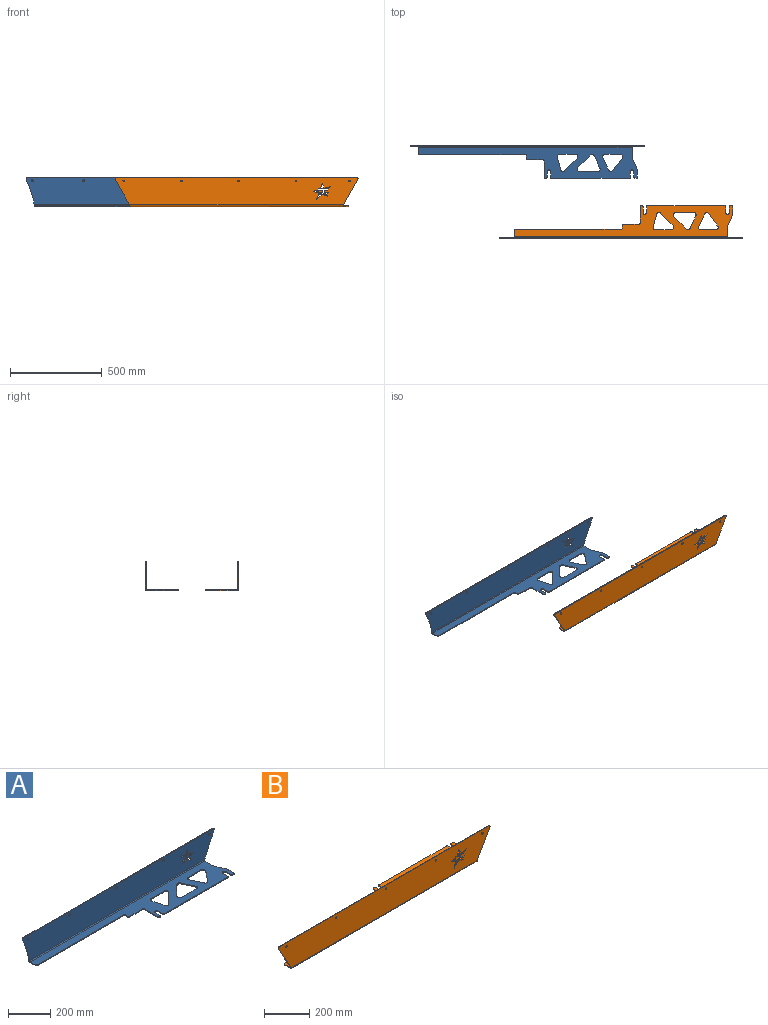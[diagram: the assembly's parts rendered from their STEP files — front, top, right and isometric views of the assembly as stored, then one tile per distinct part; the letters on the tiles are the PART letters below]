
ASSEMBLY  parts=2 mates=1
PART A: 100 faces, bbox 1277.8x189x159.2 mm
  f0: plane 86.55x4.83mm, normal (0,-1,0), area 417.7mm2, adj f1,f82,f91,f94
  f1: cylinder r=12.7mm len=21.68mm, axis (0,0,1), area 144.4mm2, adj f0,f2,f91,f94
  f2: plane 68.26x68.26mm, normal (-0.71,0.71,0), area 465.9mm2, adj f1,f3,f91,f94
  f3: cylinder r=12.7mm len=21.25mm, axis (0,0,1), area 128.4mm2, adj f2,f4,f91,f94
  f4: plane 68.26x18.29mm, normal (0.97,0.26,0), area 341.1mm2, adj f3,f82,f91,f94
  f5: plane 68.26x68.26mm, normal (0.71,-0.71,0), area 465.9mm2, adj f6,f81,f91,f94
  f6: cylinder r=12.7mm len=20.49mm, axis (0,0,1), area 117.7mm2, adj f5,f7,f91,f94
  f7: plane 68.26x31.83mm, normal (-0.91,-0.42,0), area 363.5mm2, adj f6,f8,f91,f94
  f8: cylinder r=12.7mm len=18.07mm, axis (0,0,1), area 123mm2, adj f7,f9,f91,f94
  f9: plane 100.09x4.83mm, normal (0,1,0), area 483.1mm2, adj f8,f81,f91,f94
  f10: plane 84.73x4.83mm, normal (0,-1,0), area 408.9mm2, adj f11,f80,f91,f94
  f11: cylinder r=12.7mm len=20.48mm, axis (0,0,1), area 136.7mm2, adj f10,f12,f91,f94
  f12: plane 68.26x52.9mm, normal (-0.79,0.61,0), area 416.8mm2, adj f11,f13,f91,f94
  f13: cylinder r=12.7mm len=21.55mm, axis (0,0,1), area 125.4mm2, adj f12,f14,f91,f94
  f14: plane 68.26x31.83mm, normal (0.91,0.42,0), area 363.5mm2, adj f13,f80,f91,f94
  f15: plane 26.33x9.71mm, normal (-0.94,0,-0.35), area 135.4mm2, adj f16,f87,f90,f93
  f16: plane 43.9x4.83mm, normal (0,0,1), area 211.8mm2, adj f15,f17,f90,f93
  f17: plane 11.2x10.3mm, normal (0.68,0,0.74), area 73.4mm2, adj f16,f18,f90,f93
  f18: plane 34.33x8.9mm, normal (-0.25,0,-0.97), area 171.2mm2, adj f17,f87,f90,f93
  f19: plane 5.93x5.89mm, normal (-0.71,0,-0.7), area 40.3mm2, adj f20,f86,f90,f93
  f20: plane 13.79x4.83mm, normal (-1,0,0), area 66.5mm2, adj f19,f21,f90,f93
  f21: plane 5.74x5.7mm, normal (-0.7,0,0.71), area 39.1mm2, adj f20,f22,f90,f93
  f22: plane 17.91x4.83mm, normal (0,0,1), area 86.4mm2, adj f21,f23,f90,f93
  f23: plane 5.7x5.67mm, normal (0.71,0,0.7), area 38.8mm2, adj f22,f24,f90,f93
  f24: plane 21.53x4.83mm, normal (0,0,-1), area 103.9mm2, adj f23,f25,f90,f93
  f25: plane 13.79x4.83mm, normal (1,0,0), area 66.5mm2, adj f24,f26,f90,f93
  f26: plane 15.97x4.83mm, normal (0,0,1), area 77.1mm2, adj f25,f27,f90,f93
  f27: plane 6.45x5.93mm, normal (0.68,0,0.74), area 42.3mm2, adj f26,f86,f90,f93
  f28: plane 26.46x8.9mm, normal (-0.95,0,-0.32), area 134.7mm2, adj f29,f85,f90,f93
  f29: plane 28.68x24.95mm, normal (0.66,0,0.75), area 183.4mm2, adj f28,f30,f90,f93
  f30: plane 27.88x9.37mm, normal (-0.32,0,0.95), area 142mm2, adj f29,f31,f90,f93
  f31: plane 10.88x4.83mm, normal (0.94,0,-0.35), area 56.1mm2, adj f30,f85,f90,f93
  f32: plane 18.1x6.82mm, normal (-0.35,0,0.94), area 93.3mm2, adj f33,f84,f90,f93
  f33: plane 12.28x4.83mm, normal (1,0,0), area 59.2mm2, adj f32,f84,f90,f93
  f34: plane 16.77x4.83mm, normal (0,0,-1), area 80.9mm2, adj f35,f83,f90,f93
  f35: plane 13.79x4.83mm, normal (1,0,0), area 66.5mm2, adj f34,f36,f90,f93
  f36: plane 16.77x4.83mm, normal (0,0,1), area 80.9mm2, adj f35,f37,f90,f93
  f37: plane 5.93x5.93mm, normal (0.71,0,0.71), area 40.5mm2, adj f36,f38,f90,f93
  f38: plane 24.68x4.83mm, normal (0,0,-1), area 119.1mm2, adj f37,f39,f90,f93
  f39: plane 5.93x5.93mm, normal (-0.71,0,-0.71), area 40.5mm2, adj f38,f40,f90,f93
  f40: plane 13.77x4.83mm, normal (-1,0,0), area 66.5mm2, adj f39,f41,f90,f93
  f41: plane 5.72x5.72mm, normal (-0.71,0,0.71), area 39mm2, adj f40,f42,f90,f93
  f42: plane 24.7x4.83mm, normal (0,0,1), area 119.2mm2, adj f41,f83,f90,f93
  f43: cylinder r=6.35mm len=6.35mm, axis (0,0,-1), area 48.1mm2, adj f44,f88,f91,f94
  f44: plane 576.26x4.83mm, normal (0,-1,0), area 2781mm2, adj f43,f45,f91,f94
  f45: cylinder r=6.35mm len=6.35mm, axis (0,0,1), area 48.1mm2, adj f44,f46,f91,f94
  f46: plane 15.88x4.83mm, normal (-1,0,0), area 76.6mm2, adj f45,f47,f91,f94
  f47: cylinder r=6.35mm len=6.35mm, axis (0,0,-1), area 48.1mm2, adj f46,f48,f91,f94
  f48: plane 85.73x4.83mm, normal (0,-1,0), area 413.7mm2, adj f47,f49,f91,f94
  f49: cylinder r=6.35mm len=6.35mm, axis (0,0,1), area 48.1mm2, adj f48,f50,f91,f94
  f50: plane 88.9x4.83mm, normal (-1,0,0), area 429mm2, adj f49,f51,f91,f94
  f51: cylinder r=6.35mm len=6.35mm, axis (0,0,-1), area 48.1mm2, adj f50,f52,f91,f94
  f52: plane 4.83x1.7mm, normal (0,-1,0), area 8.2mm2, adj f51,f53,f91,f94
  f53: cylinder r=6.35mm len=6.35mm, axis (0,0,1), area 48.1mm2, adj f52,f54,f91,f94
  f54: plane 31.17x4.83mm, normal (1,0,0), area 150.4mm2, adj f53,f55,f91,f94
  f55: cylinder r=9.53mm len=19.05mm, axis (0,0,1), area 144.4mm2, adj f54,f56,f91,f94
  f56: plane 31.17x4.83mm, normal (-1,0,0), area 150.4mm2, adj f55,f57,f91,f94
  f57: cylinder r=6.35mm len=6.35mm, axis (0,0,1), area 48.1mm2, adj f56,f58,f91,f94
  f58: plane 421.53x4.83mm, normal (0,-1,0), area 2034.3mm2, adj f57,f59,f91,f94
  f59: cylinder r=6.35mm len=6.35mm, axis (0,0,1), area 48.1mm2, adj f58,f60,f91,f94
  f60: plane 31.17x4.83mm, normal (1,0,0), area 150.4mm2, adj f59,f61,f91,f94
  f61: cylinder r=9.53mm len=19.05mm, axis (0,0,1), area 144.4mm2, adj f60,f62,f91,f94
  f62: plane 31.17x4.83mm, normal (-1,0,0), area 150.4mm2, adj f61,f63,f91,f94
  f63: cylinder r=6.35mm len=6.35mm, axis (0,0,-1), area 48.1mm2, adj f62,f64,f91,f94
  f64: plane 6.35x4.83mm, normal (0,-1,0), area 30.6mm2, adj f63,f65,f91,f94
  f65: cylinder r=6.35mm len=6.35mm, axis (0,0,-1), area 48.1mm2, adj f64,f66,f91,f94
  f66: plane 31.7x4.83mm, normal (1,0,0), area 153mm2, adj f65,f67,f91,f94
  f67: cylinder r=50.8mm len=20.66mm, axis (0,0,-1), area 102.7mm2, adj f66,f68,f91,f94
  f68: plane 44.45x19.79mm, normal (0.91,0.41,0), area 234.8mm2, adj f67,f69,f91,f94
  f69: cylinder r=50.8mm len=20.66mm, axis (0,0,1), area 102.7mm2, adj f68,f70,f91,f94
  f70: plane 46.04x4.83mm, normal (1,0,0), area 222.2mm2, adj f69,f71,f91,f94
  f71: bspline ~38.35x19.18mm, area 56.3mm2, adj f70,f72,f89,f92
  f72: plane 4.83x2.43mm, normal (0.87,0,-0.48), area 13.4mm2, adj f71,f73,f90,f93
  f73: cylinder r=2408.89mm len=137.99mm, axis (0,-1,0), area 733.8mm2, adj f72,f74,f90,f93
  f74: cylinder r=6.35mm len=9.2mm, axis (0,-1,0), area 62.4mm2, adj f73,f75,f90,f93
  f75: plane 1265.05x4.83mm, normal (0,0,1), area 6105.2mm2, adj f74,f76,f90,f93
  f76: cylinder r=6.35mm len=9.11mm, axis (0,-1,0), area 61.9mm2, adj f75,f77,f90,f93
  f77: cylinder r=539.84mm len=118.91mm, axis (0,1,0), area 608.6mm2, adj f76,f78,f90,f93
  f78: plane 21.59x4.83mm, normal (-0.99,0,-0.11), area 104.8mm2, adj f77,f79,f90,f93
  f79: bspline ~19.18x19.18mm, area 54.5mm2, adj f78,f88,f89,f92
  f80: cylinder r=12.7mm len=18.07mm, axis (0,0,1), area 123mm2, adj f10,f14,f91,f94
  f81: cylinder r=12.7mm len=21.68mm, axis (0,0,1), area 144.4mm2, adj f5,f9,f91,f94
  f82: cylinder r=12.7mm len=15.99mm, axis (0,0,1), area 112.3mm2, adj f0,f4,f91,f94
  f83: plane 5.74x5.7mm, normal (0.7,0,-0.71), area 39.1mm2, adj f34,f42,f90,f93
  f84: plane 18.1x5.46mm, normal (-0.29,0,-0.96), area 91.2mm2, adj f32,f33,f90,f93
  f85: plane 43.58x4.83mm, normal (0,0,-1), area 210.3mm2, adj f28,f31,f90,f93
  f86: plane 24.32x4.83mm, normal (0,0,-1), area 117.4mm2, adj f19,f27,f90,f93
  f87: plane 24.92x11.05mm, normal (0.91,0,-0.41), area 131.6mm2, adj f15,f18,f90,f93
  f88: plane 33.34x4.83mm, normal (-1,0,0), area 160.9mm2, adj f43,f79,f91,f94
  f89: cylinder r=4.76mm len=1167.77mm, axis (1,0,0), area 8720.8mm2, adj f71,f79,f90,f91
  f90: plane 1277.75x149.61mm, normal (0,-1,0), area 180359.1mm2, adj f15,f16,f17,f18,f19,f20,f21,f22
  f91: plane 1193.17x169.86mm, normal (0,0,1), area 91109.6mm2, adj f0,f1,f2,f3,f4,f5,f6,f7
  f92: cylinder r=9.59mm len=1167.77mm, axis (1,0,0), area 17558mm2, adj f71,f79,f93,f94
  f93: plane 1277.75x149.61mm, normal (0,1,0), area 179289.2mm2, adj f15,f16,f17,f18,f19,f20,f21,f22
  f94: plane 1193.17x169.86mm, normal (0,0,-1), area 91109.6mm2, adj f0,f1,f2,f3,f4,f5,f6,f7
  f95: cone r=10.01mm half-angle=42deg, axis (0,1,0), area 319.8mm2, adj f90,f93
  f96: cone r=10.01mm half-angle=42deg, axis (0,1,0), area 319.8mm2, adj f90,f93
  f97: cone r=10.01mm half-angle=42deg, axis (0,1,0), area 319.8mm2, adj f90,f93
  f98: cone r=10.01mm half-angle=42deg, axis (0,1,0), area 319.8mm2, adj f90,f93
  f99: cone r=10.01mm half-angle=42deg, axis (0,1,0), area 319.8mm2, adj f90,f93
PART B: 102 faces, bbox 1322.2x179.4x159.1 mm
  f0: plane 27.44x4.76mm, normal (1,0,0), area 130.7mm2, adj f27,f28,f50,f96
  f1: plane 33.34x4.76mm, normal (-1,0,0), area 158.8mm2, adj f2,f27,f28,f97
  f2: cylinder r=6.35mm len=6.35mm, axis (0,0,1), area 47.5mm2, adj f1,f3,f27,f28
  f3: plane 576.26x4.76mm, normal (0,1,0), area 2744.5mm2, adj f2,f4,f27,f28
  f4: cylinder r=6.35mm len=6.35mm, axis (0,0,-1), area 47.5mm2, adj f3,f5,f27,f28
  f5: plane 15.88x4.76mm, normal (-1,0,0), area 75.6mm2, adj f4,f6,f27,f28
  f6: cylinder r=6.35mm len=6.35mm, axis (0,0,1), area 47.5mm2, adj f5,f7,f27,f28
  f7: plane 85.73x4.76mm, normal (0,1,0), area 408.3mm2, adj f6,f8,f27,f28
  f8: cylinder r=6.35mm len=6.35mm, axis (0,0,-1), area 47.5mm2, adj f7,f9,f27,f28
  f9: plane 88.9x4.76mm, normal (-1,0,0), area 423.4mm2, adj f8,f10,f27,f28
  f10: cylinder r=6.35mm len=6.35mm, axis (0,0,1), area 47.5mm2, adj f9,f11,f27,f28
  f11: plane 4.76x1.7mm, normal (0,1,0), area 8.1mm2, adj f10,f27,f28,f30
  f12: plane 31.17x4.76mm, normal (1,0,0), area 148.5mm2, adj f13,f27,f28,f30
  f13: cylinder r=9.53mm len=19.05mm, axis (0,0,-1), area 142.5mm2, adj f12,f14,f27,f28
  f14: plane 31.17x4.76mm, normal (-1,0,0), area 148.5mm2, adj f13,f27,f28,f31
  f15: plane 418.99x4.76mm, normal (0,1,0), area 1995.4mm2, adj f27,f28,f29,f31
  f16: plane 31.17x4.76mm, normal (1,0,0), area 148.5mm2, adj f17,f27,f28,f29
  f17: cylinder r=9.53mm len=19.05mm, axis (0,0,-1), area 142.5mm2, adj f16,f18,f27,f28
  f18: plane 31.17x4.76mm, normal (-1,0,0), area 148.5mm2, adj f17,f19,f27,f28
  f19: cylinder r=6.35mm len=6.35mm, axis (0,0,1), area 47.5mm2, adj f18,f20,f27,f28
  f20: plane 6.35x4.76mm, normal (0,1,0), area 30.2mm2, adj f19,f21,f27,f28
  f21: cylinder r=6.35mm len=6.35mm, axis (0,0,1), area 47.5mm2, adj f20,f22,f27,f28
  f22: plane 31.7x4.76mm, normal (1,0,0), area 151mm2, adj f21,f23,f27,f28
  f23: cylinder r=50.8mm len=20.66mm, axis (0,0,1), area 101.3mm2, adj f22,f24,f27,f28
  f24: plane 44.45x19.79mm, normal (0.91,-0.41,0), area 231.7mm2, adj f23,f25,f27,f28
  f25: cylinder r=50.8mm len=20.66mm, axis (0,0,-1), area 101.3mm2, adj f24,f26,f27,f28
  f26: plane 18.6x4.76mm, normal (1,0,0), area 88.6mm2, adj f25,f27,f28,f50
  f27: plane 1190.63x169.86mm, normal (0,0,-1), area 90816mm2, adj f0,f1,f2,f3,f4,f5,f6,f7
  f28: plane 1190.63x169.86mm, normal (0,0,1), area 90816mm2, adj f0,f1,f2,f3,f4,f5,f6,f7
  f29: cylinder r=6.35mm len=6.35mm, axis (0,0,-1), area 47.5mm2, adj f15,f16,f27,f28
  f30: cylinder r=6.35mm len=6.35mm, axis (0,0,-1), area 47.5mm2, adj f11,f12,f27,f28
  f31: cylinder r=6.35mm len=6.35mm, axis (0,0,-1), area 47.5mm2, adj f14,f15,f27,f28
  f32: cylinder r=12.7mm len=21.25mm, axis (0,0,-1), area 126.7mm2, adj f27,f28,f33,f37
  f33: plane 68.26x18.29mm, normal (0.97,-0.26,0), area 336.6mm2, adj f27,f28,f32,f34
  f34: cylinder r=12.7mm len=15.99mm, axis (0,0,-1), area 110.8mm2, adj f27,f28,f33,f35
  f35: plane 86.55x4.76mm, normal (0,1,0), area 412.2mm2, adj f27,f28,f34,f36
  f36: cylinder r=12.7mm len=21.68mm, axis (0,0,-1), area 142.5mm2, adj f27,f28,f35,f37
  f37: plane 68.26x68.26mm, normal (-0.71,-0.71,0), area 459.8mm2, adj f27,f28,f32,f36
  f38: cylinder r=12.7mm len=18.07mm, axis (0,0,-1), area 121.4mm2, adj f27,f28,f39,f43
  f39: plane 100.09x4.76mm, normal (0,-1,0), area 476.7mm2, adj f27,f28,f38,f40
  f40: cylinder r=12.7mm len=21.68mm, axis (0,0,-1), area 142.5mm2, adj f27,f28,f39,f41
  f41: plane 68.26x68.26mm, normal (0.71,0.71,0), area 459.8mm2, adj f27,f28,f40,f42
  f42: cylinder r=12.7mm len=20.49mm, axis (0,0,-1), area 116.1mm2, adj f27,f28,f41,f43
  f43: plane 68.26x31.83mm, normal (-0.91,0.42,0), area 358.7mm2, adj f27,f28,f38,f42
  f44: cylinder r=12.7mm len=21.73mm, axis (0,0,-1), area 125.2mm2, adj f27,f28,f45,f49
  f45: plane 68.26x31.83mm, normal (0.91,-0.42,0), area 358.7mm2, adj f27,f28,f44,f46
  f46: cylinder r=12.7mm len=18.07mm, axis (0,0,-1), area 121.4mm2, adj f27,f28,f45,f47
  f47: plane 82.19x4.76mm, normal (0,1,0), area 391.4mm2, adj f27,f28,f46,f48
  f48: cylinder r=12.7mm len=20.24mm, axis (0,0,-1), area 133.5mm2, adj f27,f28,f47,f49
  f49: plane 68.26x50.36mm, normal (-0.8,-0.59,0), area 404mm2, adj f27,f28,f44,f48
  f50: plane 4.76x0.02mm, normal (0,-1,0), area 0.1mm2, adj f0,f26,f27,f28
  f51: extruded ~108.67x59.55mm, area 590.2mm2, adj f92,f94,f95,f100
  f52: plane 1309.48x4.76mm, normal (0,0,1), area 6236.4mm2, adj f92,f94,f100,f101
  f53: extruded ~138.06x78.01mm, area 755.2mm2, adj f92,f93,f94,f101
  f54: cylinder r=4.83mm len=9.65mm, axis (0,-1,0), area 144.4mm2, adj f92,f94
  f55: cylinder r=4.83mm len=9.65mm, axis (0,-1,0), area 144.4mm2, adj f92,f94
  f56: cylinder r=4.83mm len=9.65mm, axis (0,-1,0), area 144.4mm2, adj f92,f94
  f57: cylinder r=4.83mm len=9.65mm, axis (0,-1,0), area 144.4mm2, adj f92,f94
  f58: cylinder r=4.83mm len=9.65mm, axis (0,-1,0), area 144.4mm2, adj f92,f94
  f59: plane 17.47x4.76mm, normal (0,0,1), area 83.2mm2, adj f60,f68,f92,f94
  f60: plane 6.18x6.18mm, normal (-0.71,0,0.71), area 41.6mm2, adj f59,f61,f92,f94
  f61: plane 25.71x4.76mm, normal (0,0,-1), area 122.4mm2, adj f60,f62,f92,f94
  f62: plane 6.18x6.18mm, normal (0.71,0,-0.71), area 41.6mm2, adj f61,f63,f92,f94
  f63: plane 14.35x4.76mm, normal (1,0,0), area 68.3mm2, adj f62,f64,f92,f94
  f64: plane 5.96x5.96mm, normal (0.71,0,0.71), area 40.1mm2, adj f63,f65,f92,f94
  f65: plane 25.73x4.76mm, normal (0,0,1), area 122.5mm2, adj f64,f66,f92,f94
  f66: plane 5.98x5.94mm, normal (-0.7,0,-0.71), area 40.2mm2, adj f65,f67,f92,f94
  f67: plane 17.47x4.76mm, normal (0,0,-1), area 83.2mm2, adj f66,f68,f92,f94
  f68: plane 14.36x4.76mm, normal (-1,0,0), area 68.4mm2, adj f59,f67,f92,f94
  f69: plane 18.85x5.68mm, normal (0.29,0,-0.96), area 93.8mm2, adj f70,f71,f92,f94
  f70: plane 18.85x7.1mm, normal (0.35,0,0.94), area 95.9mm2, adj f69,f71,f92,f94
  f71: plane 12.79x4.76mm, normal (-1,0,0), area 60.9mm2, adj f69,f70,f92,f94
  f72: plane 11.67x10.73mm, normal (-0.68,0,0.74), area 75.5mm2, adj f73,f76,f92,f94
  f73: plane 35.76x9.27mm, normal (0.25,0,-0.97), area 175.9mm2, adj f72,f74,f92,f94
  f74: plane 25.96x11.51mm, normal (-0.91,0,-0.41), area 135.3mm2, adj f73,f75,f92,f94
  f75: plane 27.43x10.12mm, normal (0.94,0,-0.35), area 139.2mm2, adj f74,f76,f92,f94
  f76: plane 45.72x4.76mm, normal (0,0,1), area 217.8mm2, adj f72,f75,f92,f94
  f77: plane 29.04x9.77mm, normal (0.32,0,0.95), area 145.9mm2, adj f78,f81,f92,f94
  f78: plane 11.34x4.76mm, normal (-0.94,0,-0.35), area 57.7mm2, adj f77,f79,f92,f94
  f79: plane 45.39x4.76mm, normal (0,0,-1), area 216.2mm2, adj f78,f80,f92,f94
  f80: plane 27.56x9.27mm, normal (0.95,0,-0.32), area 138.5mm2, adj f79,f81,f92,f94
  f81: plane 29.87x25.99mm, normal (-0.66,0,0.75), area 188.6mm2, adj f77,f80,f92,f94
  f82: plane 5.98x5.94mm, normal (0.7,0,0.71), area 40.2mm2, adj f83,f91,f92,f94
  f83: plane 18.66x4.76mm, normal (0,0,1), area 88.9mm2, adj f82,f84,f92,f94
  f84: plane 5.94x5.9mm, normal (-0.71,0,0.7), area 39.9mm2, adj f83,f85,f92,f94
  f85: plane 22.43x4.76mm, normal (0,0,-1), area 106.8mm2, adj f84,f86,f92,f94
  f86: plane 14.36x4.76mm, normal (-1,0,0), area 68.4mm2, adj f85,f87,f92,f94
  f87: plane 16.63x4.76mm, normal (0,0,1), area 79.2mm2, adj f86,f88,f92,f94
  f88: plane 6.72x6.18mm, normal (-0.68,0,0.74), area 43.5mm2, adj f87,f89,f92,f94
  f89: plane 25.33x4.76mm, normal (0,0,-1), area 120.6mm2, adj f88,f90,f92,f94
  f90: plane 6.18x6.14mm, normal (0.71,0,-0.7), area 41.5mm2, adj f89,f91,f92,f94
  f91: plane 14.36x4.76mm, normal (1,0,0), area 68.4mm2, adj f82,f90,f92,f94
  f92: plane 1322.18x149.61mm, normal (0,-1,0), area 184253.3mm2, adj f51,f52,f53,f54,f55,f56,f57,f58
  f93: plane 4.76x2.03mm, normal (1,0,0), area 9.6mm2, adj f53,f92,f94,f96
  f94: plane 1322.18x149.61mm, normal (0,1,0), area 184253.3mm2, adj f51,f52,f53,f54,f55,f56,f57,f58
  f95: plane 31.4x18.13mm, normal (-0.87,0,-0.5), area 172.7mm2, adj f51,f92,f94,f97
  f96: plane 9.53x9.53mm, normal (1,0,0), area 53.4mm2, adj f0,f93,f98,f99
  f97: bspline ~9.53x9.53mm, area 55.6mm2, adj f1,f95,f98,f99
  f98: cylinder r=9.53mm len=1164.78mm, axis (1,0,0), area 17406.7mm2, adj f27,f92,f96,f97
  f99: cylinder r=4.76mm len=1164.78mm, axis (1,0,0), area 8703.3mm2, adj f28,f94,f96,f97
  f100: cylinder r=6.35mm len=9.53mm, axis (0,-1,0), area 63.4mm2, adj f51,f52,f92,f94
  f101: cylinder r=6.35mm len=9.52mm, axis (0,-1,0), area 63.3mm2, adj f52,f53,f92,f94
PLACE A t=(-400.9,-595.44,-243.24)mm
PLACE B t=(120.28,-1092.38,-243.3)mm
MATE planar B.f27 <-> A.f94  axis (0,0,-1) through (285.64,-1022.68,-248.06)mm
